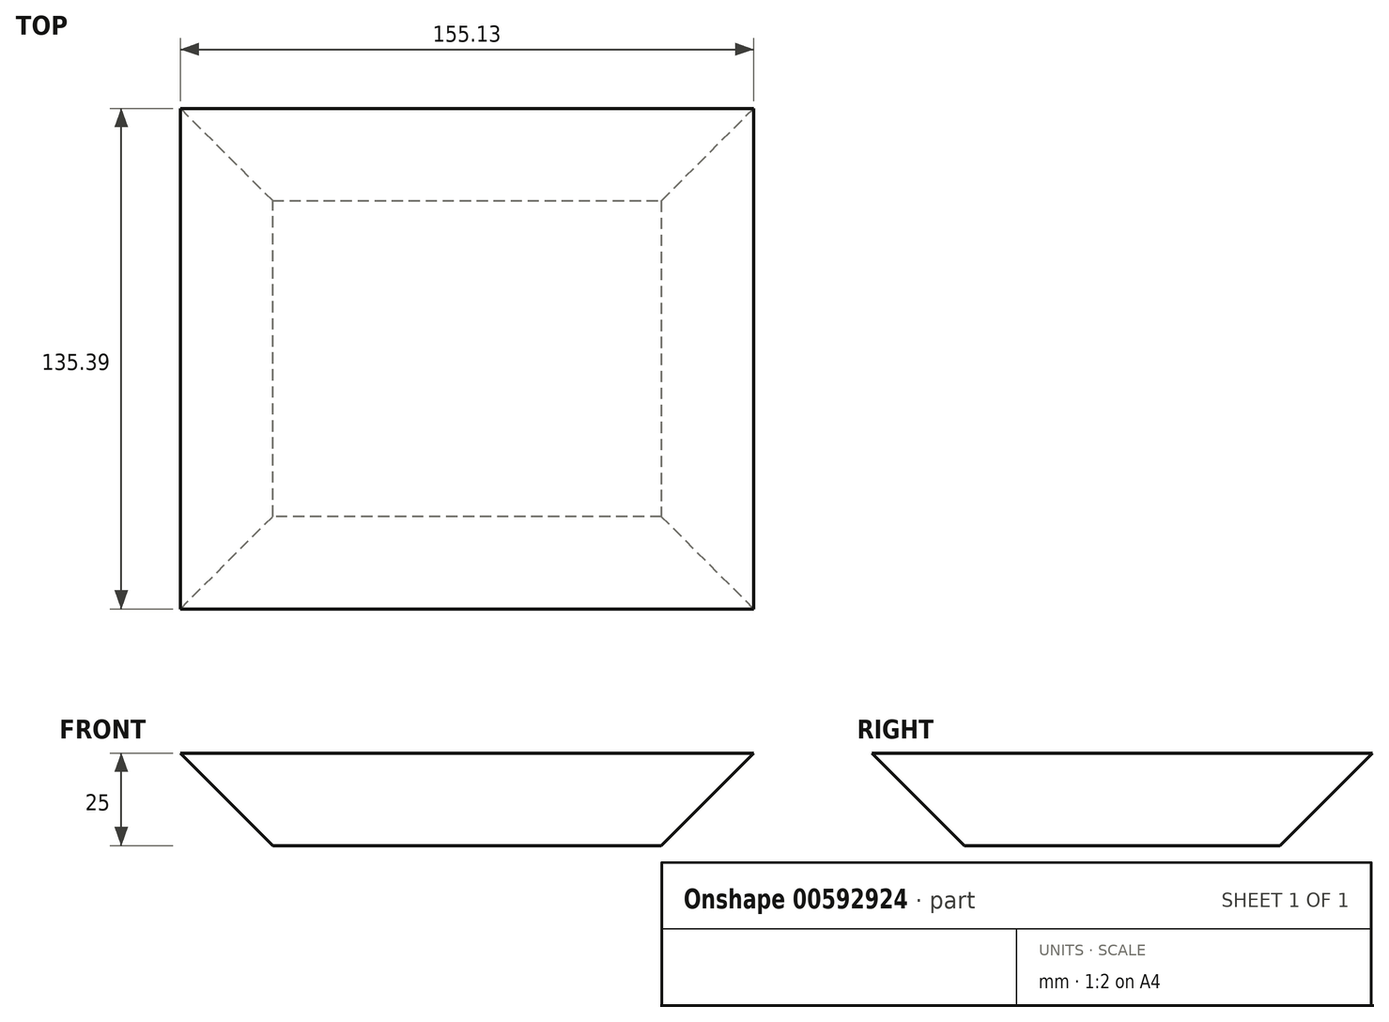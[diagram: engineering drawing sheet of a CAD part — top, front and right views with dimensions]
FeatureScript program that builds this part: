
annotation { "Feature Type Name" : "Feature", "Feature Type Description" : "" }
export const myFeature = defineFeature(function(context is Context, id is Id, definition is map)
    precondition{}
    {
        {
            var Q0;
            Q0=qCreatedBy(makeId("Top.planeOp"),FACE);
            var sketch = newSketch(context, id + "F0", { "sketchPlane" : qUnion([Q0])});
            skLineSegment(sketch, "E0.bottom", {"start": v(-43.99, 39.2) * mm, "end": v(61.14, 39.2) * mm});
            skLineSegment(sketch, "E0.top", {"start": v(-43.99, -46.2) * mm, "end": v(61.14, -46.2) * mm});
            skLineSegment(sketch, "E0.left", {"start": v(-43.99, 39.2) * mm, "end": v(-43.99, -46.2) * mm});
            skLineSegment(sketch, "E0.right", {"start": v(61.14, 39.2) * mm, "end": v(61.14, -46.2) * mm});
            skSolve(sketch);
        }
        {
            var Q0;
            Q0=makeQuery(id+"F0.imprint","IMPRINT",FACE,{"disambiguationData":[TD([[makeQuery(id+"F0.imprint","IMPRINT",EDGE,{"derivedFrom":sQuery(id+"F0.wireOp",EDGE,"E0.bottom")}),-1.0]])]});
            extrude(context, id + "F1", {"entities" : qUnion([Q0]), "depth" : 25 * mm, "offsetDistance" : 25 * mm, "hasDraft" : true, "draftAngle" : 45 * degree});
        }
    });
